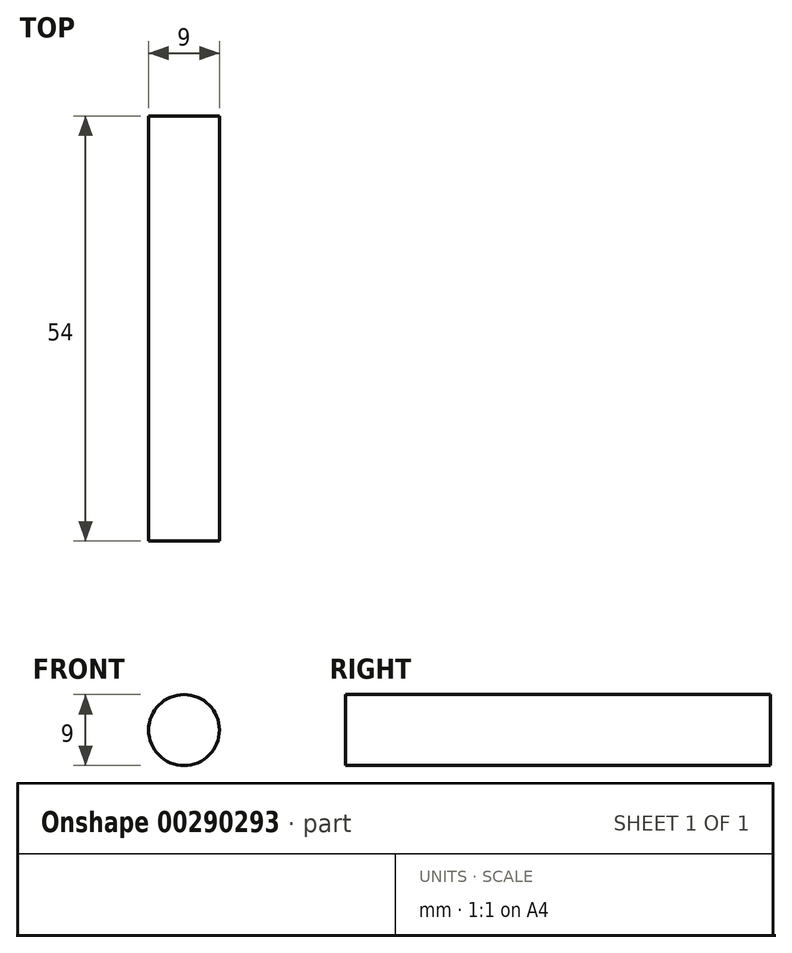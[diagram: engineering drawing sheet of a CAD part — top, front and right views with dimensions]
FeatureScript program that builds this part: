
annotation { "Feature Type Name" : "Feature", "Feature Type Description" : "" }
export const myFeature = defineFeature(function(context is Context, id is Id, definition is map)
    precondition{}
    {
        {
            var Q0;
            Q0=qCreatedBy(makeId("Front.planeOp"),FACE);
            var sketch = newSketch(context, id + "F0", { "sketchPlane" : qUnion([Q0])});
            skCircle(sketch, "E0", {"center": v(0, 0) * mm, "radius": 4.5 * mm});
            skSolve(sketch);
        }
        {
            var Q0;
            Q0 = qSketchRegion(id + "F0", true);
            extrude(context, id + "F1", {"entities" : qUnion([Q0]), "depth" : 54 * mm});
        }
    });
